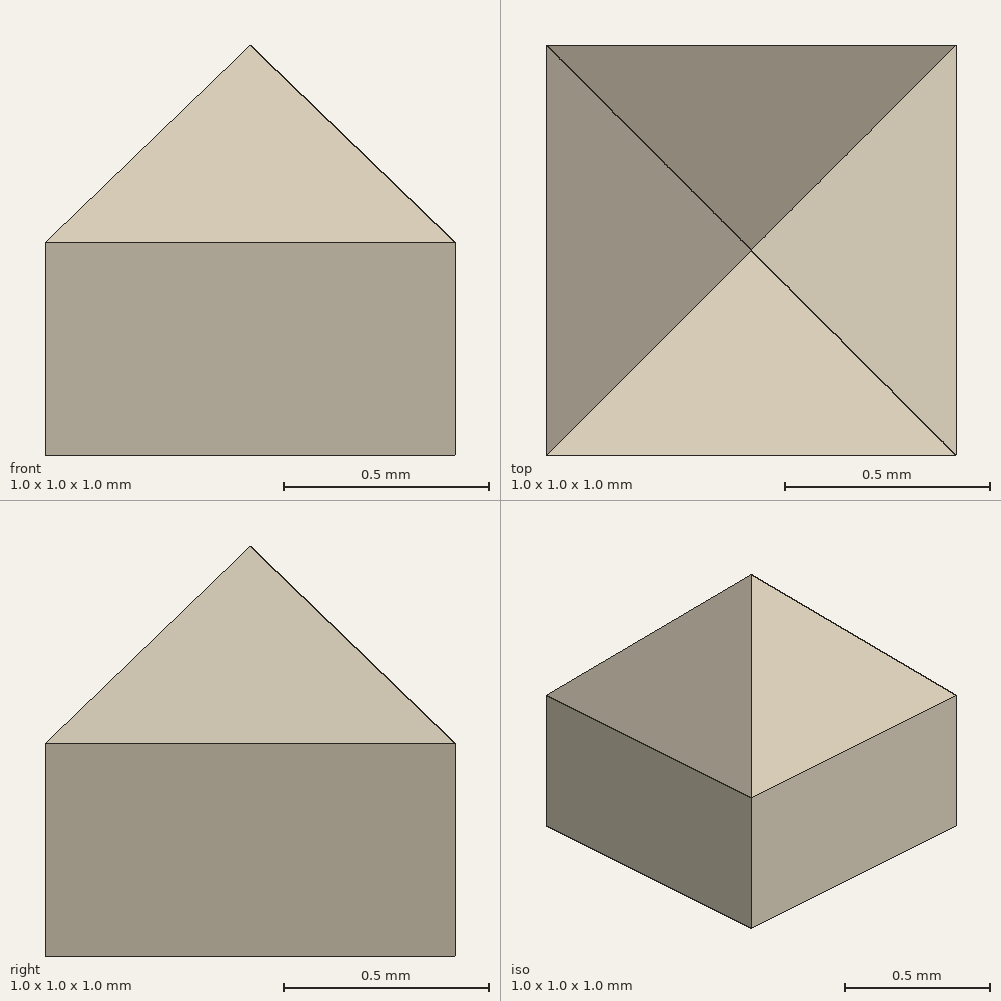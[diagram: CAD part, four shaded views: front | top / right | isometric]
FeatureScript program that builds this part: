
annotation { "Feature Type Name" : "Feature", "Feature Type Description" : "" }
export const myFeature = defineFeature(function(context is Context, id is Id, definition is map)
    precondition{}
    {
        {
            var Q0;
            Q0=qCreatedBy(makeId("Top.planeOp"),FACE);
            var sketch = newSketch(context, id + "F0", { "sketchPlane" : qUnion([Q0])});
            skLineSegment(sketch, "E0.bottom", {"start": v(0, 0) * mm, "end": v(1, 0) * mm});
            skLineSegment(sketch, "E0.top", {"start": v(0, 1) * mm, "end": v(1, 1) * mm});
            skLineSegment(sketch, "E0.left", {"start": v(0, 0) * mm, "end": v(0, 1) * mm});
            skLineSegment(sketch, "E0.right", {"start": v(1, 0) * mm, "end": v(1, 1) * mm});
            skSolve(sketch);
        }
        {
            var Q0;
            Q0=makeQuery(id+"F0.imprint","IMPRINT",FACE,{"disambiguationData":[TD([[makeQuery(id+"F0.imprint","IMPRINT",EDGE,{"derivedFrom":sQuery(id+"F0.wireOp",EDGE,"E0.bottom")}),1.0]])]});
            extrude(context, id + "F1", {"entities" : qUnion([Q0]), "depth" : 1 * mm, "offsetDistance" : 25 * mm});
        }
        {
            var Q0;
            Q0=makeQuery(id+"F1.opExtrude","SWEPT_FACE",FACE,{"disambiguationData":[OSD([sQuery(id+"F0.wireOp",EDGE,"E0.top")])]});
            var sketch = newSketch(context, id + "F2", { "sketchPlane" : qUnion([Q0])});
            skLineSegment(sketch, "E1", {"start": v(-1, 0.52) * mm, "end": v(0, 0.52) * mm});
            skLineSegment(sketch, "E2", {"start": v(-1, 0.52) * mm, "end": v(-0.5, 1) * mm});
            skLineSegment(sketch, "E3", {"start": v(0, 0.52) * mm, "end": v(-0.5, 1) * mm});
            skSolve(sketch);
        }
        {
            var Q0;
            Q0=makeQuery(id+"F1.opExtrude","SWEPT_FACE",FACE,{"disambiguationData":[OSD([sQuery(id+"F0.wireOp",EDGE,"E0.right")])]});
            var sketch = newSketch(context, id + "F3", { "sketchPlane" : qUnion([Q0])});
            skLineSegment(sketch, "E4", {"start": v(0, 0.52) * mm, "end": v(1, 0.52) * mm});
            skLineSegment(sketch, "E5", {"start": v(1, 0.52) * mm, "end": v(0.5, 1) * mm});
            skLineSegment(sketch, "E6", {"start": v(0.5, 1) * mm, "end": v(0, 0.52) * mm});
            skSolve(sketch);
        }
        {
            var Q0;
            {var subQ0=sQuery(id+"F2.wireOp",EDGE,"E2");Q0=makeQuery(id+"F2.imprint","IMPRINT",FACE,{"disambiguationData":[TD([[makeQuery(id+"F2.imprint","IMPRINT",EDGE,{"derivedFrom":subQ0}),1.0]])]});}
            var Q1;
            {var subQ0=sQuery(id+"F2.wireOp",EDGE,"E3");Q1=makeQuery(id+"F2.imprint","IMPRINT",FACE,{"disambiguationData":[TD([[makeQuery(id+"F2.imprint","IMPRINT",EDGE,{"derivedFrom":subQ0}),-1.0]])]});}
            extrude(context, id + "F4", {"entities" : qUnion([Q0, Q1]), "operationType" : NewBodyOperationType.REMOVE, "oppositeDirection" : true, "depth" : 25 * mm, "offsetDistance" : 25 * mm});
        }
        {
            var Q0;
            {var subQ0=sQuery(id+"F3.wireOp",EDGE,"E5");Q0=makeQuery(id+"F3.imprint","IMPRINT",FACE,{"disambiguationData":[TD([[makeQuery(id+"F3.imprint","IMPRINT",EDGE,{"derivedFrom":subQ0}),-1.0]])]});}
            var Q1;
            {var subQ0=sQuery(id+"F3.wireOp",EDGE,"E6");Q1=makeQuery(id+"F3.imprint","IMPRINT",FACE,{"disambiguationData":[TD([[makeQuery(id+"F3.imprint","IMPRINT",EDGE,{"derivedFrom":subQ0}),-1.0]])]});}
            extrude(context, id + "F5", {"entities" : qUnion([Q0, Q1]), "operationType" : NewBodyOperationType.REMOVE, "oppositeDirection" : true, "depth" : 25 * mm, "offsetDistance" : 25 * mm});
        }
    });
